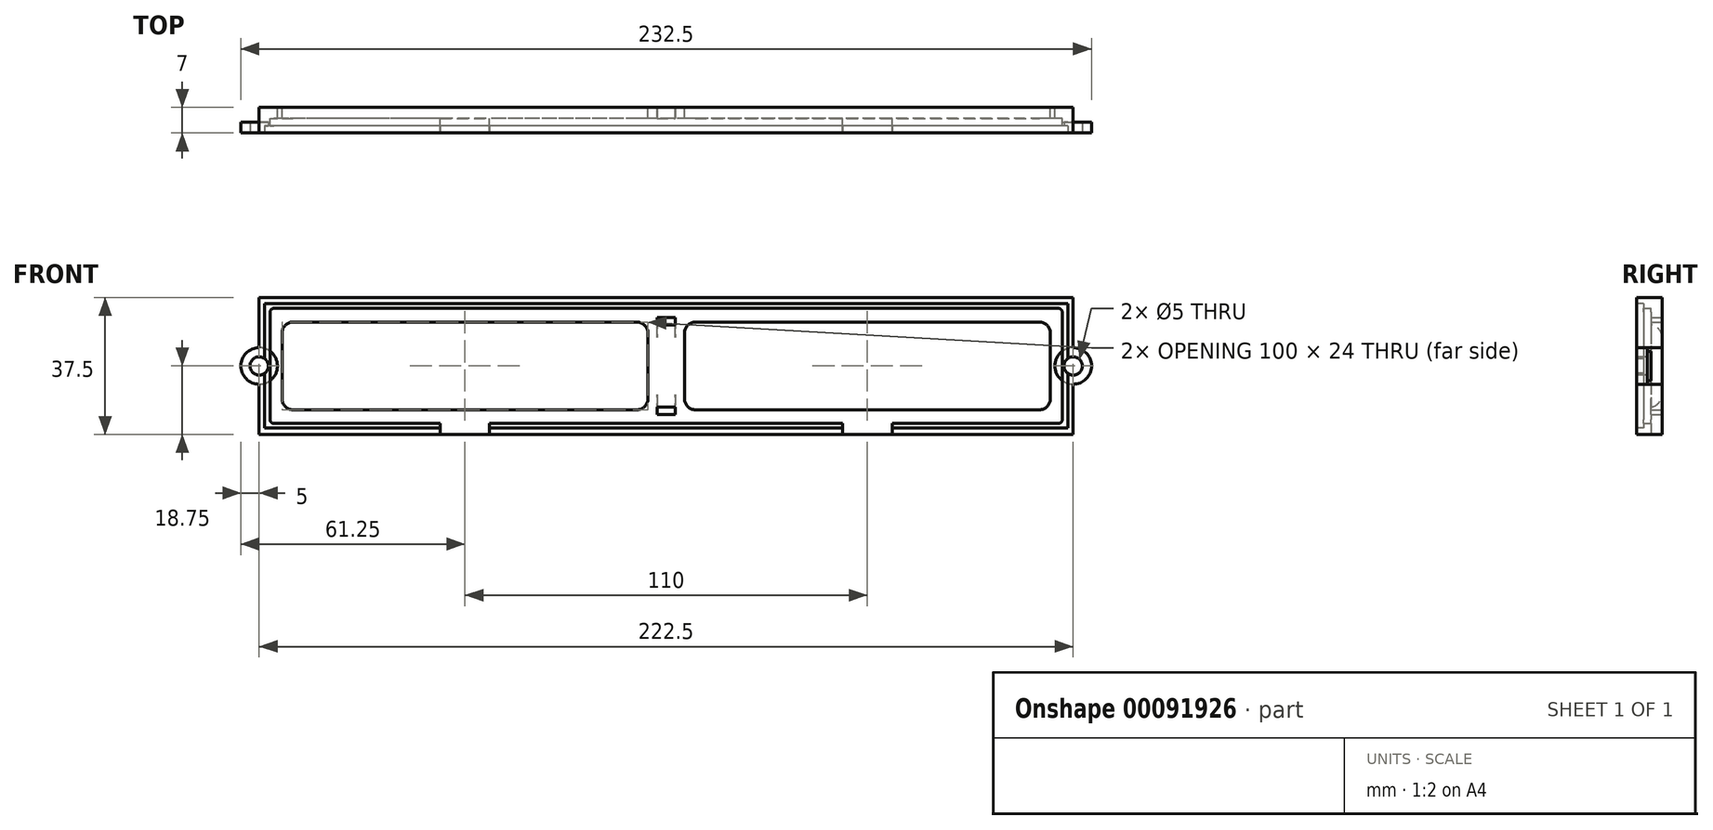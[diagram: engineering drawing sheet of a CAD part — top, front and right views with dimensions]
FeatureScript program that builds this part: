
annotation { "Feature Type Name" : "Feature", "Feature Type Description" : "" }
export const myFeature = defineFeature(function(context is Context, id is Id, definition is map)
    precondition{}
    {
        {
            var Q0;
            Q0=qCreatedBy(makeId("Front.planeOp"),FACE);
            var sketch = newSketch(context, id + "F0", { "sketchPlane" : qUnion([Q0])});
            skLineSegment(sketch, "E0.bottom", {"start": v(111.25, 18.75) * mm, "end": v(-111.25, 18.75) * mm});
            skLineSegment(sketch, "E0.top", {"start": v(111.25, -18.75) * mm, "end": v(-111.25, -18.75) * mm});
            skLineSegment(sketch, "E0.left", {"start": v(111.25, 18.75) * mm, "end": v(111.25, -18.75) * mm});
            skLineSegment(sketch, "E0.right", {"start": v(-111.25, 18.75) * mm, "end": v(-111.25, -18.75) * mm});
            skPoint(sketch, "E0.middle", {"position": v(0, 0) * mm});
            skLineSegment(sketch, "E1.bottom", {"start": v(-8, 12) * mm, "end": v(-102, 12) * mm});
            skLineSegment(sketch, "E1.top", {"start": v(-8, -12) * mm, "end": v(-102, -12) * mm});
            skLineSegment(sketch, "E1.left", {"start": v(-5, 9) * mm, "end": v(-5, -9) * mm});
            skLineSegment(sketch, "E1.right", {"start": v(-105, 9) * mm, "end": v(-105, -9) * mm});
            skPoint(sketch, "E1.middle", {"position": v(-55, 0) * mm});
            skPoint(sketch, "E2.visualSharp", {"position": v(-105, 12) * mm});
            skArc(sketch, "E2.filletArc", {"start": v(-102, 12) * mm, "mid": v(-104.12, 11.12) * mm, "end": v(-105, 9) * mm});
            skPoint(sketch, "E3.visualSharp", {"position": v(-5, 12) * mm});
            skArc(sketch, "E3.filletArc", {"start": v(-5, 9) * mm, "mid": v(-5.88, 11.12) * mm, "end": v(-8, 12) * mm});
            skPoint(sketch, "E4.visualSharp", {"position": v(-5, -12) * mm});
            skArc(sketch, "E4.filletArc", {"start": v(-8, -12) * mm, "mid": v(-5.88, -11.12) * mm, "end": v(-5, -9) * mm});
            skPoint(sketch, "E5.visualSharp", {"position": v(-105, -12) * mm});
            skArc(sketch, "E5.filletArc", {"start": v(-105, -9) * mm, "mid": v(-104.12, -11.12) * mm, "end": v(-102, -12) * mm});
            skArc(sketch, "E6.MirrorCS", {"start": v(102, 12) * mm, "mid": v(104.12, 11.12) * mm, "end": v(105, 9) * mm});
            skArc(sketch, "E7.MirrorCS", {"start": v(5, 9) * mm, "mid": v(5.88, 11.12) * mm, "end": v(8, 12) * mm});
            skArc(sketch, "E8.MirrorCS", {"start": v(8, -12) * mm, "mid": v(5.88, -11.12) * mm, "end": v(5, -9) * mm});
            skArc(sketch, "E9.MirrorCS", {"start": v(105, -9) * mm, "mid": v(104.12, -11.12) * mm, "end": v(102, -12) * mm});
            skLineSegment(sketch, "E10.MirrorCS", {"start": v(8, -12) * mm, "end": v(102, -12) * mm});
            skPoint(sketch, "E11.MirrorP", {"position": v(105, -12) * mm});
            skLineSegment(sketch, "E12.MirrorCS", {"start": v(5, 9) * mm, "end": v(5, -9) * mm});
            skLineSegment(sketch, "E13.MirrorCS", {"start": v(8, 12) * mm, "end": v(102, 12) * mm});
            skLineSegment(sketch, "E14.MirrorCS", {"start": v(105, 9) * mm, "end": v(105, -9) * mm});
            skPoint(sketch, "E15.MirrorP", {"position": v(5, 12) * mm});
            skPoint(sketch, "E16.MirrorP", {"position": v(105, 12) * mm});
            skPoint(sketch, "E17.MirrorP", {"position": v(55, 0) * mm});
            skPoint(sketch, "E18.MirrorP", {"position": v(5, -12) * mm});
            skArc(sketch, "E19", {"start": v(-111.25, -5) * mm, "mid": v(-116.25, 0) * mm, "end": v(-111.25, 5) * mm});
            skArc(sketch, "E20.MirrorCS", {"start": v(111.25, -5) * mm, "mid": v(116.25, 0) * mm, "end": v(111.25, 5) * mm});
            skLineSegment(sketch, "E21.bottom", {"start": v(-2.5, 13.25) * mm, "end": v(2.5, 13.25) * mm});
            skLineSegment(sketch, "E21.top", {"start": v(-2.5, 11.25) * mm, "end": v(2.5, 11.25) * mm});
            skLineSegment(sketch, "E21.left", {"start": v(-2.5, 13.25) * mm, "end": v(-2.5, 11.25) * mm});
            skLineSegment(sketch, "E21.right", {"start": v(2.5, 13.25) * mm, "end": v(2.5, 11.25) * mm});
            skPoint(sketch, "E21.middle", {"position": v(0, 12.25) * mm});
            skLineSegment(sketch, "E22.MirrorCS", {"start": v(2.5, -13.25) * mm, "end": v(2.5, -11.25) * mm});
            skLineSegment(sketch, "E23.MirrorCS", {"start": v(-2.5, -13.25) * mm, "end": v(2.5, -13.25) * mm});
            skLineSegment(sketch, "E24.MirrorCS", {"start": v(-2.5, -11.25) * mm, "end": v(2.5, -11.25) * mm});
            skLineSegment(sketch, "E25.MirrorCS", {"start": v(-2.5, -13.25) * mm, "end": v(-2.5, -11.25) * mm});
            skPoint(sketch, "E26.MirrorP", {"position": v(0, -12.25) * mm});
            skSolve(sketch);
        }
        {
            var Q0;
            Q0=qSketchRegion(id+"F0",true);
            extrude(context, id + "F1", {"entities" : qUnion([Q0]), "depth" : 3 * mm});
        }
        {
            var Q0;
            Q0=makeQuery(id+"F1.opExtrude","CAP_FACE",FACE,{"disambiguationData":[OSD([sQuery(id+"F0.wireOp",EDGE,"E0.bottom"),sQuery(id+"F0.wireOp",EDGE,"E0.top"),sQuery(id+"F0.wireOp",EDGE,"E0.left"),sQuery(id+"F0.wireOp",EDGE,"E0.right"),sQuery(id+"F0.wireOp",EDGE,"E1.bottom"),sQuery(id+"F0.wireOp",EDGE,"E1.top"),sQuery(id+"F0.wireOp",EDGE,"E1.left"),sQuery(id+"F0.wireOp",EDGE,"E1.right"),sQuery(id+"F0.wireOp",EDGE,"E2.filletArc"),sQuery(id+"F0.wireOp",EDGE,"E3.filletArc"),sQuery(id+"F0.wireOp",EDGE,"E4.filletArc"),sQuery(id+"F0.wireOp",EDGE,"E5.filletArc"),sQuery(id+"F0.wireOp",EDGE,"E6.MirrorCS"),sQuery(id+"F0.wireOp",EDGE,"E7.MirrorCS"),sQuery(id+"F0.wireOp",EDGE,"E8.MirrorCS"),sQuery(id+"F0.wireOp",EDGE,"E9.MirrorCS"),sQuery(id+"F0.wireOp",EDGE,"E10.MirrorCS"),sQuery(id+"F0.wireOp",EDGE,"E12.MirrorCS"),sQuery(id+"F0.wireOp",EDGE,"E13.MirrorCS"),sQuery(id+"F0.wireOp",EDGE,"E14.MirrorCS")])],"isStart":false});
            var sketch = newSketch(context, id + "F2", { "sketchPlane" : qUnion([Q0])});
            skLineSegment(sketch, "E27.bottom", {"start": v(107.25, 15.75) * mm, "end": v(-107.25, 15.75) * mm});
            skLineSegment(sketch, "E27.top", {"start": v(107.25, -15.75) * mm, "end": v(-107.25, -15.75) * mm});
            skLineSegment(sketch, "E27.left", {"start": v(108.25, 14.75) * mm, "end": v(108.25, -14.75) * mm});
            skLineSegment(sketch, "E27.right", {"start": v(-108.25, 14.75) * mm, "end": v(-108.25, -14.75) * mm});
            skPoint(sketch, "E28.visualSharp", {"position": v(-108.25, 15.75) * mm});
            skArc(sketch, "E28.filletArc", {"start": v(-107.25, 15.75) * mm, "mid": v(-107.96, 15.46) * mm, "end": v(-108.25, 14.75) * mm});
            skPoint(sketch, "E29.visualSharp", {"position": v(108.25, 15.75) * mm});
            skArc(sketch, "E29.filletArc", {"start": v(108.25, 14.75) * mm, "mid": v(107.96, 15.46) * mm, "end": v(107.25, 15.75) * mm});
            skPoint(sketch, "E30.visualSharp", {"position": v(108.25, -15.75) * mm});
            skArc(sketch, "E30.filletArc", {"start": v(107.25, -15.75) * mm, "mid": v(107.96, -15.46) * mm, "end": v(108.25, -14.75) * mm});
            skPoint(sketch, "E31.visualSharp", {"position": v(-108.25, -15.75) * mm});
            skArc(sketch, "E31.filletArc", {"start": v(-108.25, -14.75) * mm, "mid": v(-107.96, -15.46) * mm, "end": v(-107.25, -15.75) * mm});
            skCircle(sketch, "E32", {"center": v(-111.25, 0) * mm, "radius": 2 * mm});
            skCircle(sketch, "E33.MirrorC", {"center": v(111.25, 0) * mm, "radius": 2 * mm});
            skSolve(sketch);
        }
        {
            var Q0;
            Q0=makeQuery(id+"F2.imprint","IMPRINT",FACE,{"disambiguationData":[TD([[makeQuery(id+"F2.imprint","IMPRINT",EDGE,{"derivedFrom":sQuery(id+"F2.wireOp",EDGE,"E27.bottom")}),-1.0]])]});
            var Q1;
            Q1=makeQuery(id+"F2.imprint","IMPRINT",FACE,{"disambiguationData":[TD([[makeQuery(id+"F2.imprint","IMPRINT",EDGE,{"derivedFrom":sQuery(id+"F2.wireOp",EDGE,"8UQ35Aj4-GzFw-aaHB-QqC8-tIVl76PQ1ExV")}),1.0]])]});
            extrude(context, id + "F3", {"entities" : qUnion([Q0, Q1]), "operationType" : NewBodyOperationType.ADD, "depth" : 4 * mm});
        }
        {
            var Q0;
            Q0=makeQuery(id+"F3.opExtrude","CAP_FACE",FACE,{"disambiguationData":[OSD([sQuery(id+"F0.wireOp",EDGE,"E0.bottom"),sQuery(id+"F0.wireOp",EDGE,"E0.top"),sQuery(id+"F0.wireOp",EDGE,"E0.left"),sQuery(id+"F0.wireOp",EDGE,"E0.right"),sQuery(id+"F0.wireOp",EDGE,"E19"),sQuery(id+"F0.wireOp",EDGE,"E20.MirrorCS"),sQuery(id+"F2.wireOp",EDGE,"E27.bottom"),sQuery(id+"F2.wireOp",EDGE,"E27.top"),sQuery(id+"F2.wireOp",EDGE,"E27.left"),sQuery(id+"F2.wireOp",EDGE,"E27.right"),sQuery(id+"F2.wireOp",EDGE,"E28.filletArc"),sQuery(id+"F2.wireOp",EDGE,"E29.filletArc"),sQuery(id+"F2.wireOp",EDGE,"E30.filletArc"),sQuery(id+"F2.wireOp",EDGE,"E31.filletArc"),sQuery(id+"F2.wireOp",EDGE,"E32"),sQuery(id+"F2.wireOp",EDGE,"E33.MirrorC")])],"isStart":false});
            var sketch = newSketch(context, id + "F4", { "sketchPlane" : qUnion([Q0])});
            skLineSegment(sketch, "E34.bottom", {"start": v(109.75, 17) * mm, "end": v(-109.75, 17) * mm});
            skLineSegment(sketch, "E34.top", {"start": v(109.75, -17) * mm, "end": v(-109.75, -17) * mm});
            skLineSegment(sketch, "E34.left", {"start": v(109.75, 17) * mm, "end": v(109.75, -17) * mm});
            skLineSegment(sketch, "E34.right", {"start": v(-109.75, 17) * mm, "end": v(-109.75, -17) * mm});
            skPoint(sketch, "E34.middle", {"position": v(0, 0) * mm});
            skLineSegment(sketch, "E35.bottom", {"start": v(107.27, 14.5) * mm, "end": v(-107.27, 14.5) * mm});
            skLineSegment(sketch, "E35.top", {"start": v(107.27, -14.5) * mm, "end": v(-107.27, -14.5) * mm});
            skLineSegment(sketch, "E35.left", {"start": v(107.27, 14.5) * mm, "end": v(107.27, -14.5) * mm});
            skLineSegment(sketch, "E35.right", {"start": v(-107.27, 14.5) * mm, "end": v(-107.27, -14.5) * mm});
            skSolve(sketch);
        }
        {
            var Q0;
            Q0 = qSketchRegion(id + "F4", true);
            extrude(context, id + "F5", {"entities" : qUnion([Q0]), "operationType" : NewBodyOperationType.REMOVE, "oppositeDirection" : true, "depth" : 2 * mm});
        }
        {
            var Q0;
            Q0=makeQuery(id+"F3.opExtrude","CAP_FACE",FACE,{"disambiguationData":[OSD([sQuery(id+"F0.wireOp",EDGE,"E0.bottom"),sQuery(id+"F0.wireOp",EDGE,"E0.top"),sQuery(id+"F0.wireOp",EDGE,"E0.left"),sQuery(id+"F0.wireOp",EDGE,"E0.right"),sQuery(id+"F0.wireOp",EDGE,"E19"),sQuery(id+"F0.wireOp",EDGE,"E20.MirrorCS"),sQuery(id+"F2.wireOp",EDGE,"E27.bottom"),sQuery(id+"F2.wireOp",EDGE,"E27.top"),sQuery(id+"F2.wireOp",EDGE,"E27.left"),sQuery(id+"F2.wireOp",EDGE,"E27.right"),sQuery(id+"F2.wireOp",EDGE,"E28.filletArc"),sQuery(id+"F2.wireOp",EDGE,"E29.filletArc"),sQuery(id+"F2.wireOp",EDGE,"E30.filletArc"),sQuery(id+"F2.wireOp",EDGE,"E31.filletArc"),sQuery(id+"F2.wireOp",EDGE,"E32"),sQuery(id+"F2.wireOp",EDGE,"E33.MirrorC")])],"isStart":false});
            var sketch = newSketch(context, id + "F6", { "sketchPlane" : qUnion([Q0])});
            skCircle(sketch, "E36", {"center": v(-111.25, 0) * mm, "radius": 2.5 * mm});
            skCircle(sketch, "E37.MirrorC", {"center": v(111.25, 0) * mm, "radius": 2.5 * mm});
            skSolve(sketch);
        }
        {
            var Q0;
            Q0 = qSketchRegion(id + "F6", true);
            extrude(context, id + "F7", {"entities" : qUnion([Q0]), "operationType" : NewBodyOperationType.REMOVE, "endBound" : BoundingType.THROUGH_ALL, "oppositeDirection" : true, "depth" : 25 * mm});
        }
        {
            var Q0;
            Q0=makeQuery(id+"F1.opExtrude","CAP_FACE",FACE,{"disambiguationData":[OSD([sQuery(id+"F0.wireOp",EDGE,"E0.bottom"),sQuery(id+"F0.wireOp",EDGE,"E0.top"),sQuery(id+"F0.wireOp",EDGE,"E0.left"),sQuery(id+"F0.wireOp",EDGE,"E0.right"),sQuery(id+"F0.wireOp",EDGE,"E1.bottom"),sQuery(id+"F0.wireOp",EDGE,"E1.top"),sQuery(id+"F0.wireOp",EDGE,"E1.left"),sQuery(id+"F0.wireOp",EDGE,"E1.right"),sQuery(id+"F0.wireOp",EDGE,"E2.filletArc"),sQuery(id+"F0.wireOp",EDGE,"E3.filletArc"),sQuery(id+"F0.wireOp",EDGE,"E4.filletArc"),sQuery(id+"F0.wireOp",EDGE,"E5.filletArc"),sQuery(id+"F0.wireOp",EDGE,"E6.MirrorCS"),sQuery(id+"F0.wireOp",EDGE,"E7.MirrorCS"),sQuery(id+"F0.wireOp",EDGE,"E8.MirrorCS"),sQuery(id+"F0.wireOp",EDGE,"E9.MirrorCS"),sQuery(id+"F0.wireOp",EDGE,"E10.MirrorCS"),sQuery(id+"F0.wireOp",EDGE,"E12.MirrorCS"),sQuery(id+"F0.wireOp",EDGE,"E13.MirrorCS"),sQuery(id+"F0.wireOp",EDGE,"E14.MirrorCS"),sQuery(id+"F0.wireOp",EDGE,"E19"),sQuery(id+"F0.wireOp",EDGE,"E20.MirrorCS")])],"isStart":true});
            var sketch = newSketch(context, id + "F8", { "sketchPlane" : qUnion([Q0])});
            skCircle(sketch, "E38", {"center": v(-111.25, 0) * mm, "radius": 5 * mm});
            skCircle(sketch, "E39.MirrorC", {"center": v(111.25, 0) * mm, "radius": 5 * mm});
            skSolve(sketch);
        }
        {
            var Q0;
            Q0 = qSketchRegion(id + "F8", true);
            extrude(context, id + "F9", {"entities" : qUnion([Q0]), "operationType" : NewBodyOperationType.REMOVE, "oppositeDirection" : true, "depth" : 4 * mm});
        }
        {
            var Q0;
            {var subQ0=sQuery(id+"F0.wireOp",EDGE,"E0.top");Q0=makeQuery(id+"F3.boolean.opBoolean","MERGE",FACE,{"derivedFrom":[makeQuery(id+"F1.opExtrude","SWEPT_FACE",FACE,{"disambiguationData":[OSD([subQ0])]}),makeQuery(id+"F3.opExtrude","SWEPT_FACE",FACE,{"disambiguationData":[OSD([subQ0])]})]});}
            var sketch = newSketch(context, id + "F10", { "sketchPlane" : qUnion([Q0])});
            skLineSegment(sketch, "E40.bottom", {"start": v(-61.75, 7) * mm, "end": v(-48.25, 7) * mm});
            skLineSegment(sketch, "E40.top", {"start": v(-61.75, 3) * mm, "end": v(-48.25, 3) * mm});
            skLineSegment(sketch, "E40.left", {"start": v(-61.75, 7) * mm, "end": v(-61.75, 3) * mm});
            skLineSegment(sketch, "E40.right", {"start": v(-48.25, 7) * mm, "end": v(-48.25, 3) * mm});
            skPoint(sketch, "E41", {"position": v(-55, 3) * mm});
            skPoint(sketch, "E42.MirrorP", {"position": v(55, 3) * mm});
            skLineSegment(sketch, "E43.MirrorCS", {"start": v(61.75, 7) * mm, "end": v(48.25, 7) * mm});
            skLineSegment(sketch, "E44.MirrorCS", {"start": v(61.75, 3) * mm, "end": v(48.25, 3) * mm});
            skLineSegment(sketch, "E45.MirrorCS", {"start": v(48.25, 7) * mm, "end": v(48.25, 3) * mm});
            skLineSegment(sketch, "E46.MirrorCS", {"start": v(61.75, 7) * mm, "end": v(61.75, 3) * mm});
            skSolve(sketch);
        }
        {
            var Q0;
            Q0 = qSketchRegion(id + "F10", true);
            extrude(context, id + "F11", {"entities" : qUnion([Q0]), "operationType" : NewBodyOperationType.REMOVE, "oppositeDirection" : true, "depth" : 25 * mm});
        }
        {
            var Q0;
            Q0=makeQuery(id+"F1.opExtrude","CAP_EDGE",EDGE,{"disambiguationData":[OSD([sQuery(id+"F0.wireOp",EDGE,"E21.top")])],"isStart":true});
            var Q1;
            Q1=makeQuery(id+"F1.opExtrude","CAP_EDGE",EDGE,{"disambiguationData":[OSD([sQuery(id+"F0.wireOp",EDGE,"E24.MirrorCS")])],"isStart":true});
            fillet(context, id + "F12", {"entities" : qUnion([Q0, Q1]), "radius" : 3.5 * mm, "tangentPropagation" : true, "allowEdgeOverflow" : false});
        }
    });
